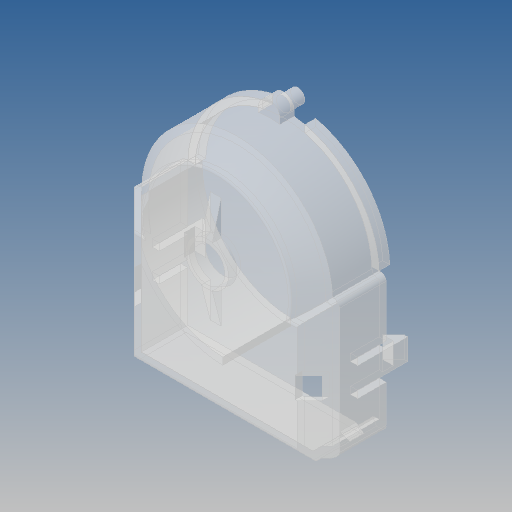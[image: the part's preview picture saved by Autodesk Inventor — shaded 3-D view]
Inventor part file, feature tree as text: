
AUTODESK INVENTOR PART (.ipt)
format: ipt  version: 2020 (Build 240168000, 168)  size: 246,784 bytes
history: mixed  units: mm
features: other x5, fillet x1, imported_body x1
ambient origin geometry x8: Origin, YZ Plane, XZ Plane, XY Plane, X Axis, Y Axis, Z Axis, Center Point
bodies: Body1 (imported_parasolid), Body2 (imported_parasolid), Body3 (imported_parasolid)
feature tree (7):
  other  "Твердое тело1"
  other  "Твердое тело2"
  other  "Твердое тело3"
  fillet  "Fillet3"  [1 undecoded]
  other  "Boss-Extrude37[1]"
  other  "Boss-Extrude37[2]"
  imported_body  NMx_Import_Brep_tag  [imported B-rep: ~70 faces, bbox_mm=[28.8, 34.559862, 9.71967]]
note: 1 required parameter value undecoded (feature->parameter linkage not recoverable at this tier; creation-order binding heuristic only, values carry confidence <= 0.55)
